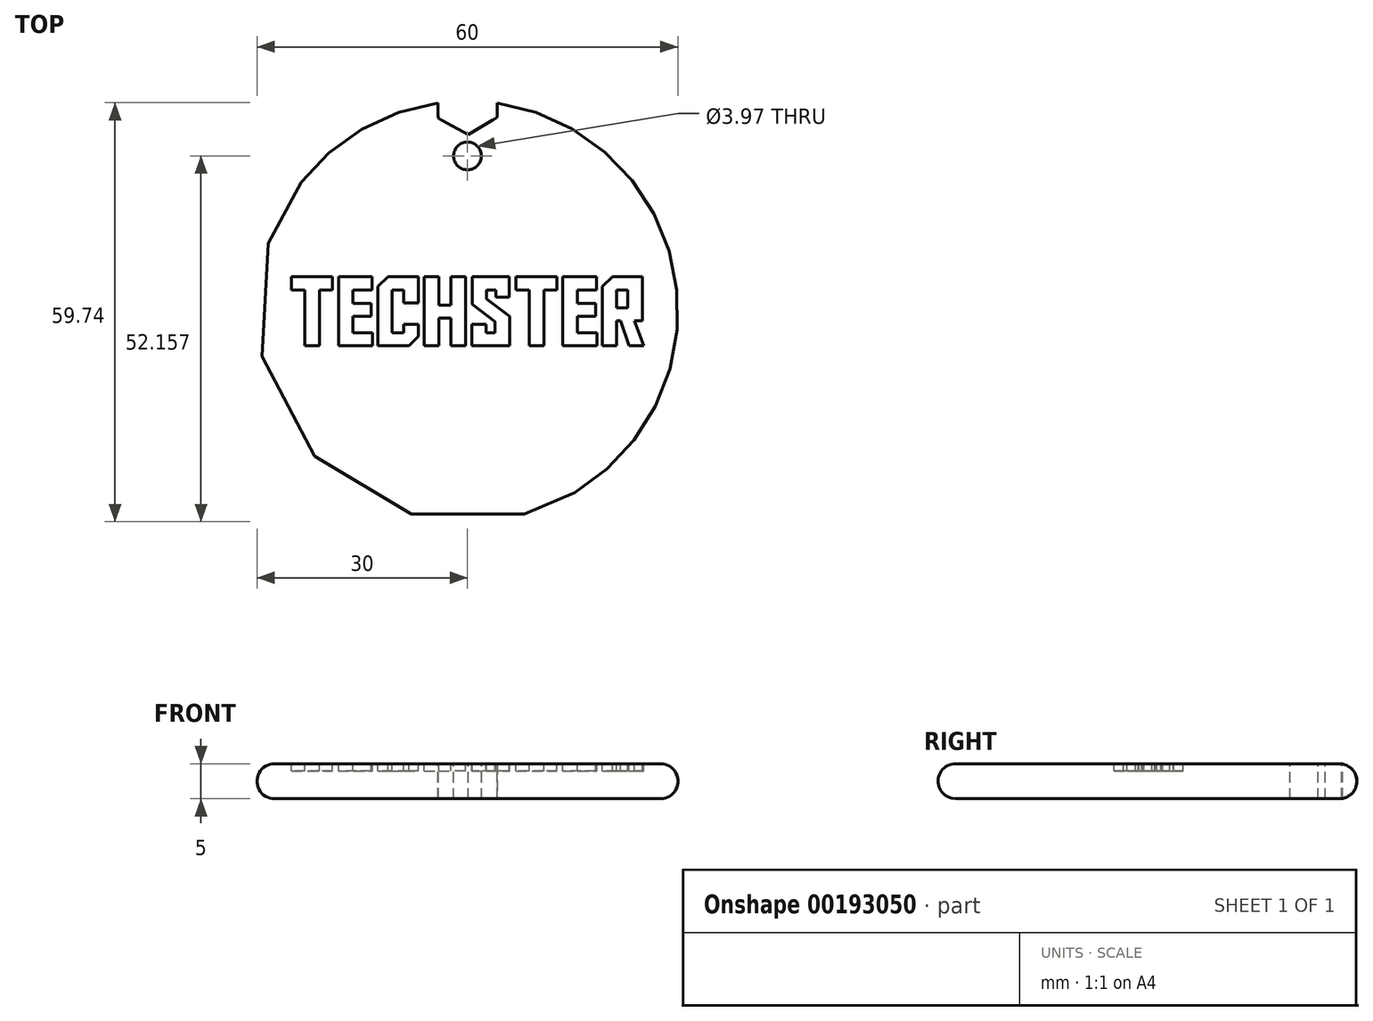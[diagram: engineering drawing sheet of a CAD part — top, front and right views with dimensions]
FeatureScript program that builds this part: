
annotation { "Feature Type Name" : "Feature", "Feature Type Description" : "" }
export const myFeature = defineFeature(function(context is Context, id is Id, definition is map)
    precondition{}
    {
        {
            var Q0;
            Q0=qCreatedBy(makeId("Front.planeOp"),FACE);
            var sketch = newSketch(context, id + "F0", { "sketchPlane" : qUnion([Q0])});
            skLineSegment(sketch, "E0.bottom", {"start": v(0, 0) * mm, "end": v(-27.5, 0) * mm});
            skLineSegment(sketch, "E0.top", {"start": v(0, 5) * mm, "end": v(-27.5, 5) * mm});
            skLineSegment(sketch, "E0.left", {"start": v(0, 0) * mm, "end": v(0, 5) * mm});
            skLineSegment(sketch, "E0.right", {"start": v(-27.5, 0) * mm, "end": v(-27.5, 5) * mm});
            skArc(sketch, "E1", {"start": v(-27.5, 5) * mm, "mid": v(-30, 2.5) * mm, "end": v(-27.5, 0) * mm});
            skSolve(sketch);
        }
        {
            var Q0;
            Q0 = qSketchRegion(id + "F0", true);
            var Q1;
            Q1=sQuery(id+"F0.wireOp",EDGE,"E0.left");
            revolve(context, id + "F1", {"entities" : qUnion([Q0]), "axis" : qUnion([Q1]), "revolveType" : RevolveType.FULL});
        }
        {
            var Q0;
            Q0=qCreatedBy(makeId("Top.planeOp"),FACE);
            cPlane(context, id + "F2", {"entities" : qUnion([Q0]), "cplaneType" : CPlaneType.OFFSET, "offset" : 10 * mm, "width" : 152.4 * mm, "height" : 152.4 * mm});
        }
        {
            var Q0;
            Q0=qCreatedBy(id+"F2.planeOp",FACE);
            var sketch = newSketch(context, id + "F3", { "sketchPlane" : qUnion([Q0])});
            skCircle(sketch, "E2.cCircle", {"center": v(0, 30.04) * mm, "radius": 4.22 * mm, "construction": true});
            skLineSegment(sketch, "E2.0", {"start": v(4.26, 27.67) * mm, "end": v(0.08, 25.17) * mm});
            skLineSegment(sketch, "E2.1", {"start": v(0.08, 25.17) * mm, "end": v(-4.18, 27.54) * mm});
            skLineSegment(sketch, "E2.2", {"start": v(-4.18, 27.54) * mm, "end": v(-4.26, 32.4) * mm});
            skLineSegment(sketch, "E2.3", {"start": v(-4.26, 32.4) * mm, "end": v(-0.08, 34.9) * mm});
            skLineSegment(sketch, "E2.4", {"start": v(-0.08, 34.9) * mm, "end": v(4.18, 32.54) * mm});
            skLineSegment(sketch, "E2.5", {"start": v(4.18, 32.54) * mm, "end": v(4.26, 27.67) * mm});
            skPoint(sketch, "E2.0.midPoint", {"position": v(2.17, 26.42) * mm});
            skSolve(sketch);
        }
        {
            var Q0;
            Q0 = qSketchRegion(id + "F3", true);
            extrude(context, id + "F4", {"entities" : qUnion([Q0]), "operationType" : NewBodyOperationType.REMOVE, "oppositeDirection" : true, "depth" : 25.4 * mm});
        }
        {
            var Q0;
            Q0=qCreatedBy(id+"F2.planeOp",FACE);
            var sketch = newSketch(context, id + "F5", { "sketchPlane" : qUnion([Q0])});
            skCircle(sketch, "E3", {"center": v(0, 22.16) * mm, "radius": 1.98 * mm});
            skSolve(sketch);
        }
        {
            var Q0;
            Q0 = qSketchRegion(id + "F5", true);
            extrude(context, id + "F6", {"entities" : qUnion([Q0]), "operationType" : NewBodyOperationType.REMOVE, "oppositeDirection" : true, "depth" : 25.4 * mm});
        }
        {
            var Q0;
            Q0=makeQuery(id+"F1.opRevolve","SWEPT_FACE",FACE,{"disambiguationData":[OSD([sQuery(id+"F0.wireOp",EDGE,"E0.top")])]});
            var sketch = newSketch(context, id + "F7", { "sketchPlane" : qUnion([Q0])});
            skSolve(sketch);
        }
        {
            var Q0;
            {var subQ2=sQuery(id+"F0.wireOp",EDGE,"E0.top");var subQ3=makeQuery(id+"F1.opRevolve","SWEPT_FACE",FACE,{"disambiguationData":[OSD([subQ2])]});var subQ11=sQuery(id+"F3.wireOp",EDGE,"E2.0");var subQ17=makeQuery(id+"F4.opExtrude","SWEPT_FACE",FACE,{"disambiguationData":[OSD([subQ11])]});Q0=makeQuery(id+"F7.imprint","IMPRINT",FACE,{"disambiguationData":[TD([[makeQuery(id+"F7.imprint","IMPRINT",EDGE,{"derivedFrom":makeQuery(id+"F4.boolean.opBoolean","INTERSECT",EDGE,{"derivedFrom":[subQ3,subQ17]})}),-1.0]])]});}
            var sketch = newSketch(context, id + "F8", { "sketchPlane" : qUnion([Q0])});
            skLineSegment(sketch, "E4", {"start": v(-19.24, 3.05) * mm, "end": v(-21.1, 3.05) * mm});
            skLineSegment(sketch, "E5", {"start": v(-21.1, 3.05) * mm, "end": v(-21.1, -4.92) * mm});
            skLineSegment(sketch, "E6", {"start": v(-21.1, -4.92) * mm, "end": v(-23.17, -4.92) * mm});
            skLineSegment(sketch, "E7", {"start": v(-23.17, -4.92) * mm, "end": v(-23.17, 3.05) * mm});
            skLineSegment(sketch, "E8", {"start": v(-23.17, 3.05) * mm, "end": v(-25.1, 3.05) * mm});
            skLineSegment(sketch, "E9", {"start": v(-25.1, 3.05) * mm, "end": v(-25.1, 4.92) * mm});
            skLineSegment(sketch, "E10", {"start": v(-25.1, 4.92) * mm, "end": v(-19.24, 4.92) * mm});
            skLineSegment(sketch, "E11", {"start": v(-19.24, 4.92) * mm, "end": v(-19.24, 3.05) * mm});
            skLineSegment(sketch, "E12", {"start": v(-18.4, 4.92) * mm, "end": v(-13.62, 4.92) * mm});
            skLineSegment(sketch, "E13", {"start": v(-13.62, 4.92) * mm, "end": v(-13.62, 3.05) * mm});
            skLineSegment(sketch, "E14", {"start": v(-13.62, 3.05) * mm, "end": v(-16.36, 3.05) * mm});
            skLineSegment(sketch, "E15", {"start": v(-16.36, 3.05) * mm, "end": v(-16.36, 1.15) * mm});
            skLineSegment(sketch, "E16", {"start": v(-16.36, 1.15) * mm, "end": v(-13.76, 1.15) * mm});
            skLineSegment(sketch, "E17", {"start": v(-13.76, 1.15) * mm, "end": v(-13.76, -0.69) * mm});
            skLineSegment(sketch, "E18", {"start": v(-13.76, -0.69) * mm, "end": v(-16.33, -0.69) * mm});
            skLineSegment(sketch, "E19", {"start": v(-16.33, -0.69) * mm, "end": v(-16.33, -3.06) * mm});
            skLineSegment(sketch, "E20", {"start": v(-16.33, -3.06) * mm, "end": v(-13.55, -3.06) * mm});
            skLineSegment(sketch, "E21", {"start": v(-13.55, -3.06) * mm, "end": v(-13.55, -4.92) * mm});
            skLineSegment(sketch, "E22", {"start": v(-13.55, -4.92) * mm, "end": v(-18.4, -4.92) * mm});
            skLineSegment(sketch, "E23", {"start": v(-18.4, -4.92) * mm, "end": v(-18.4, 4.92) * mm});
            skLineSegment(sketch, "E24", {"start": v(-9.07, -3.06) * mm, "end": v(-9.07, -1.86) * mm});
            skLineSegment(sketch, "E25", {"start": v(-9.07, -1.86) * mm, "end": v(-7, -1.86) * mm});
            skLineSegment(sketch, "E26", {"start": v(-7, -1.86) * mm, "end": v(-7, -3.56) * mm});
            skLineSegment(sketch, "E27", {"start": v(-7, -3.56) * mm, "end": v(-8.36, -4.92) * mm});
            skLineSegment(sketch, "E28", {"start": v(-8.36, -4.92) * mm, "end": v(-12.8, -4.92) * mm});
            skLineSegment(sketch, "E29", {"start": v(-12.8, -4.92) * mm, "end": v(-12.8, 3.57) * mm});
            skLineSegment(sketch, "E30", {"start": v(-12.8, 3.57) * mm, "end": v(-11.33, 4.92) * mm});
            skLineSegment(sketch, "E31", {"start": v(-11.33, 4.92) * mm, "end": v(-7, 4.92) * mm});
            skLineSegment(sketch, "E32", {"start": v(-7, 4.92) * mm, "end": v(-7, 1.2) * mm});
            skLineSegment(sketch, "E33", {"start": v(-7, 1.2) * mm, "end": v(-9.07, 1.2) * mm});
            skLineSegment(sketch, "E34", {"start": v(-9.07, 1.2) * mm, "end": v(-9.07, 3.05) * mm});
            skLineSegment(sketch, "E35", {"start": v(-9.07, 3.05) * mm, "end": v(-10.73, 3.05) * mm});
            skLineSegment(sketch, "E36", {"start": v(-10.73, 3.05) * mm, "end": v(-10.73, -3.06) * mm});
            skLineSegment(sketch, "E37", {"start": v(-10.73, -3.06) * mm, "end": v(-9.07, -3.06) * mm});
            skLineSegment(sketch, "E38", {"start": v(-4.11, 0.88) * mm, "end": v(-2.34, 0.88) * mm});
            skLineSegment(sketch, "E39", {"start": v(-2.34, 0.88) * mm, "end": v(-2.34, 4.92) * mm});
            skLineSegment(sketch, "E40", {"start": v(-2.34, 4.92) * mm, "end": v(-0.28, 4.92) * mm});
            skLineSegment(sketch, "E41", {"start": v(-0.28, 4.92) * mm, "end": v(-0.28, -4.92) * mm});
            skLineSegment(sketch, "E42", {"start": v(-0.28, -4.92) * mm, "end": v(-2.34, -4.92) * mm});
            skLineSegment(sketch, "E43", {"start": v(-2.34, -4.92) * mm, "end": v(-2.34, -0.99) * mm});
            skLineSegment(sketch, "E44", {"start": v(-2.34, -0.99) * mm, "end": v(-4.11, -0.99) * mm});
            skLineSegment(sketch, "E45", {"start": v(-4.11, -0.99) * mm, "end": v(-4.11, -4.92) * mm});
            skLineSegment(sketch, "E46", {"start": v(-4.11, -4.92) * mm, "end": v(-6.18, -4.92) * mm});
            skLineSegment(sketch, "E47", {"start": v(-6.18, -4.92) * mm, "end": v(-6.18, 4.92) * mm});
            skLineSegment(sketch, "E48", {"start": v(-6.18, 4.92) * mm, "end": v(-4.11, 4.92) * mm});
            skLineSegment(sketch, "E49", {"start": v(-4.11, 4.92) * mm, "end": v(-4.11, 0.88) * mm});
            skLineSegment(sketch, "E50", {"start": v(6, -4.92) * mm, "end": v(0.6, -4.92) * mm});
            skLineSegment(sketch, "E51", {"start": v(0.6, -4.92) * mm, "end": v(0.6, -1.86) * mm});
            skLineSegment(sketch, "E52", {"start": v(0.6, -1.86) * mm, "end": v(2.66, -1.86) * mm});
            skLineSegment(sketch, "E53", {"start": v(2.66, -1.86) * mm, "end": v(2.66, -3.06) * mm});
            skLineSegment(sketch, "E54", {"start": v(2.66, -3.06) * mm, "end": v(3.94, -3.06) * mm});
            skLineSegment(sketch, "E55", {"start": v(3.94, -3.06) * mm, "end": v(3.94, -1.5) * mm});
            skLineSegment(sketch, "E56", {"start": v(3.94, -1.5) * mm, "end": v(0.66, 0.98) * mm});
            skLineSegment(sketch, "E57", {"start": v(0.66, 0.98) * mm, "end": v(0.66, 4.92) * mm});
            skLineSegment(sketch, "E58", {"start": v(0.66, 4.92) * mm, "end": v(5.94, 4.92) * mm});
            skLineSegment(sketch, "E59", {"start": v(5.94, 4.92) * mm, "end": v(5.94, 2) * mm});
            skLineSegment(sketch, "E60", {"start": v(5.94, 2) * mm, "end": v(4.07, 2) * mm});
            skLineSegment(sketch, "E61", {"start": v(4.07, 2) * mm, "end": v(4.07, 3.04) * mm});
            skLineSegment(sketch, "E62", {"start": v(4.07, 3.04) * mm, "end": v(2.73, 3.04) * mm});
            skLineSegment(sketch, "E63", {"start": v(2.73, 3.04) * mm, "end": v(2.73, 1.76) * mm});
            skLineSegment(sketch, "E64", {"start": v(2.73, 1.76) * mm, "end": v(6, -0.7) * mm});
            skLineSegment(sketch, "E65", {"start": v(6, -0.7) * mm, "end": v(6, -4.92) * mm});
            skLineSegment(sketch, "E66", {"start": v(12.76, 3.05) * mm, "end": v(10.9, 3.05) * mm});
            skLineSegment(sketch, "E67", {"start": v(10.9, 3.05) * mm, "end": v(10.9, -4.92) * mm});
            skLineSegment(sketch, "E68", {"start": v(10.9, -4.92) * mm, "end": v(8.82, -4.92) * mm});
            skLineSegment(sketch, "E69", {"start": v(8.82, -4.92) * mm, "end": v(8.82, 3.05) * mm});
            skLineSegment(sketch, "E70", {"start": v(8.82, 3.05) * mm, "end": v(6.9, 3.05) * mm});
            skLineSegment(sketch, "E71", {"start": v(6.9, 3.05) * mm, "end": v(6.9, 4.92) * mm});
            skLineSegment(sketch, "E72", {"start": v(6.9, 4.92) * mm, "end": v(12.76, 4.92) * mm});
            skLineSegment(sketch, "E73", {"start": v(12.76, 4.92) * mm, "end": v(12.76, 3.05) * mm});
            skLineSegment(sketch, "E74", {"start": v(13.6, 4.92) * mm, "end": v(18.37, 4.92) * mm});
            skLineSegment(sketch, "E75", {"start": v(18.37, 4.92) * mm, "end": v(18.37, 3.05) * mm});
            skLineSegment(sketch, "E76", {"start": v(18.37, 3.05) * mm, "end": v(15.64, 3.05) * mm});
            skLineSegment(sketch, "E77", {"start": v(15.64, 3.05) * mm, "end": v(15.64, 1.15) * mm});
            skLineSegment(sketch, "E78", {"start": v(15.64, 1.15) * mm, "end": v(18.24, 1.15) * mm});
            skLineSegment(sketch, "E79", {"start": v(18.24, 1.15) * mm, "end": v(18.24, -0.69) * mm});
            skLineSegment(sketch, "E80", {"start": v(18.24, -0.69) * mm, "end": v(15.66, -0.69) * mm});
            skLineSegment(sketch, "E81", {"start": v(15.66, -0.69) * mm, "end": v(15.66, -3.06) * mm});
            skLineSegment(sketch, "E82", {"start": v(15.66, -3.06) * mm, "end": v(18.44, -3.06) * mm});
            skLineSegment(sketch, "E83", {"start": v(18.44, -3.06) * mm, "end": v(18.44, -4.92) * mm});
            skLineSegment(sketch, "E84", {"start": v(18.44, -4.92) * mm, "end": v(13.6, -4.92) * mm});
            skLineSegment(sketch, "E85", {"start": v(13.6, -4.92) * mm, "end": v(13.6, 4.92) * mm});
            skLineSegment(sketch, "E86", {"start": v(23.03, -4.92) * mm, "end": v(21.8, -1.36) * mm});
            skLineSegment(sketch, "E87", {"start": v(21.8, -1.36) * mm, "end": v(21.26, -1.36) * mm});
            skLineSegment(sketch, "E88", {"start": v(21.26, -1.36) * mm, "end": v(21.26, -4.92) * mm});
            skLineSegment(sketch, "E89", {"start": v(21.26, -4.92) * mm, "end": v(19.2, -4.92) * mm});
            skLineSegment(sketch, "E90", {"start": v(19.2, -4.92) * mm, "end": v(19.2, 3.53) * mm});
            skLineSegment(sketch, "E91", {"start": v(19.2, 3.53) * mm, "end": v(20.7, 4.92) * mm});
            skLineSegment(sketch, "E92", {"start": v(20.7, 4.92) * mm, "end": v(24.9, 4.92) * mm});
            skLineSegment(sketch, "E93", {"start": v(24.9, 4.92) * mm, "end": v(24.9, -1.33) * mm});
            skLineSegment(sketch, "E94", {"start": v(24.9, -1.33) * mm, "end": v(23.79, -1.33) * mm});
            skLineSegment(sketch, "E95", {"start": v(23.79, -1.33) * mm, "end": v(25.1, -4.92) * mm});
            skLineSegment(sketch, "E96", {"start": v(25.1, -4.92) * mm, "end": v(23.03, -4.92) * mm});
            skLineSegment(sketch, "E97", {"start": v(22.84, 0.48) * mm, "end": v(22.84, 3.05) * mm});
            skLineSegment(sketch, "E98", {"start": v(22.84, 3.05) * mm, "end": v(21.26, 3.05) * mm});
            skLineSegment(sketch, "E99", {"start": v(21.26, 3.05) * mm, "end": v(21.26, 0.48) * mm});
            skLineSegment(sketch, "E100", {"start": v(21.26, 0.48) * mm, "end": v(22.84, 0.48) * mm});
            skSolve(sketch);
        }
        {
            var Q0;
            Q0 = qSketchRegion(id + "F8", true);
            extrude(context, id + "F9", {"entities" : qUnion([Q0]), "operationType" : NewBodyOperationType.REMOVE, "oppositeDirection" : true, "depth" : 1.02 * mm});
        }
    });
